# Revit family: Steel-HST Purlin-Steel & Tube-G450
name_source: partatom
category: Structural Framing
revit_build: Autodesk Revit 2018 (Build: 20170927_1515(x64)
units: mm (PartAtom-declared; Revit-internal decimal feet)

## family parameters
Always export as geometry = No
Always vertical = Yes
Cut with Voids When Loaded = No
Material for Model Behavior = Steel
OmniClass Number = 23.25.30.11.14.14
OmniClass Title = Beams
Section Shape = C Profile with Fold
Shared = No
Show family pre-cut in plan views = Yes
Structural Framing Length Roundoff = 0 mm

## types (13) — shared parameters
Assembly Code = B1020230
CBICode = 3411
CBIDescription = Structural steelwork
Coil Performance = Gauge 1.15-1.45mm; G500(MPa); 275g/m² (Zinc): Gauge 1.75-3.0mm; G450 (MPa); 275g/m²(Zinc)
Description = HST Steel Purlins and Girts are high strength lipped profile sections, providing an economic solution for your building project.
Design Instruction = All the design information should be cross referenced with the current Steel & Tube Purlins and Girts design guide, and AS/NZS 4600:2005
Design Standard = Steel & Tube’s HST purlins and Girts profiles are designed in accordance with AS/NZS 4600:2005.
Inner Fillet = 5.0 mm
Manufacturer = Steel & Tube
ManufacturerName = Steel & Tube
ManufacturerURL = http://www.steelandtube.co.nz
Material Standard = Steel & Tube’s HST purlins and Girts profiles are manufactured from materials conforming to AS1397:2011
ModifiedIssue_ANZRS = 20160330 $
Perimeter = 0.00 m²/m
Principal Axes Angle = 0.00°
Profile2 Height Validation = 152 mm  [stored 0.498688 ft]
SpecificationDescription = Steel & Tube Purlins & Girts
SpecificationReference = 3411ST
Torsional Modulus = 0.0 mm³
Type Comments = HST Steel Purlins and Girts
URL = http://www.steelandtube.co.nz
Uniclass2015Code = Pr_20_76_51_21
Uniclass2015Title = Cold-formed galvanized steel sections
Uniclass2015Version = 2015

## per-type parameters (varying)
- HST100/19: Centroid Horizontal=16.4 mm; Centroid Vertical=51.0 mm; Elastic Modulus strong axis=13140.0 mm³; Elastic Modulus weak axis=4290.0 mm³; Fold Length=10.0 mm; Height=102.0 mm; Lip Length=15.0 mm; MassPerUnitLength_ANZRS=3.23 kg/m; Moment of Inertia strong axis=658000.00 mm4; Moment of Inertia weak axis=141000.00 mm4; Nominal Weight=3.23 kgf/m; Plastic Modulus strong axis=13140.0 mm³; Plastic Modulus weak axis=4290.0 mm³; Profile1=Yes; Profile2=No; Profile23Medium=No; Profile3=No; Profile3 Height Validation=203 mm  [stored 0.66601 ft]; Section Area=400.0 mm²; SectionAreaGross_ANZRS=400.0 mm²; SectionAreaNet_ANZRS=400.0 mm²; Shear Area strong axis=400.0 mm²; Shear Area weak axis=400.0 mm²; Structural Material=Metal-Steel-450MPa; Torsional Moment of Inertia=456.00 mm4; Wall Design Thickness=1.9 mm; Wall Nominal Thickness=1.9 mm; Warping Constant=310000000.0 mm6; Width=51.0 mm; b1=8.0 mm; d1=59.0 mm; d2=10.0 mm; d3=25.0 mm; d4=48.0 mm
- HST150/18: Centroid Horizontal=23.0 mm; Centroid Vertical=76.0 mm; Elastic Modulus strong axis=27000.0 mm³; Elastic Modulus weak axis=9010.0 mm³; Fold Length=10.0 mm; Height=152.0 mm; Lip Length=24.0 mm; MassPerUnitLength_ANZRS=4.56 kg/m; Moment of Inertia strong axis=2050000.00 mm4; Moment of Inertia weak axis=364000.00 mm4; Nominal Weight=4.56 kgf/m; Plastic Modulus strong axis=27000.0 mm³; Plastic Modulus weak axis=9010.0 mm³; Profile1=No; Profile2=Yes; Profile23Medium=Yes; Profile3=No; Profile3 Height Validation=203 mm  [stored 0.66601 ft]; Section Area=578.0 mm²; SectionAreaGross_ANZRS=578.0 mm²; SectionAreaNet_ANZRS=578.0 mm²; Shear Area strong axis=578.0 mm²; Shear Area weak axis=578.0 mm²; Structural Material=Metal-Steel-450MPa; Torsional Moment of Inertia=590.00 mm4; Wall Design Thickness=1.8 mm; Wall Nominal Thickness=1.8 mm; Warping Constant=2190000000.0 mm6; Width=65.0 mm; b1=8.0 mm; d1=59.0 mm; d2=10.0 mm; d3=7.0 mm; d4=48.0 mm
- HST200/18: Centroid Horizontal=24.6 mm; Centroid Vertical=101.5 mm; Elastic Modulus strong axis=44200.0 mm³; Elastic Modulus weak axis=11900.0 mm³; Fold Length=12.0 mm; Height=203.0 mm; Lip Length=25.0 mm; MassPerUnitLength_ANZRS=5.72 kg/m; Moment of Inertia strong axis=4480000.00 mm4; Moment of Inertia weak axis=577000.00 mm4; Nominal Weight=5.72 kgf/m; Plastic Modulus strong axis=44200.0 mm³; Plastic Modulus weak axis=11900.0 mm³; Profile1=No; Profile2=No; Profile23Medium=Yes; Profile3=Yes; Profile3 Height Validation=203 mm  [stored 0.66601 ft]; Section Area=717.0 mm²; SectionAreaGross_ANZRS=717.0 mm²; SectionAreaNet_ANZRS=717.0 mm²; Shear Area strong axis=717.0 mm²; Shear Area weak axis=717.0 mm²; Structural Material=Metal-Steel-450MPa; Torsional Moment of Inertia=732.00 mm4; Wall Design Thickness=1.8 mm; Wall Nominal Thickness=1.8 mm; Warping Constant=5670000000.0 mm6; Width=75.0 mm; b1=8.0 mm; d1=59.0 mm; d2=10.0 mm; d3=10.0 mm; d4=48.0 mm
- HST250/18: Centroid Horizontal=28.3 mm; Centroid Vertical=125.0 mm; Elastic Modulus strong axis=64700.0 mm³; Elastic Modulus weak axis=16300.0 mm³; Fold Length=12.0 mm; Height=250.0 mm; Lip Length=33.0 mm; MassPerUnitLength_ANZRS=6.96 kg/m; Moment of Inertia strong axis=8090000.00 mm4; Moment of Inertia weak axis=897000.00 mm4; Nominal Weight=6.96 kgf/m; Plastic Modulus strong axis=64700.0 mm³; Plastic Modulus weak axis=16300.0 mm³; Profile1=No; Profile2=No; Profile23Medium=Yes; Profile3=Yes; Profile3 Height Validation=250 mm; Section Area=866.0 mm²; SectionAreaGross_ANZRS=866.0 mm²; SectionAreaNet_ANZRS=866.0 mm²; Shear Area strong axis=866.0 mm²; Shear Area weak axis=866.0 mm²; Structural Material=Metal-Steel-450MPa; Torsional Moment of Inertia=885.00 mm4; Wall Design Thickness=1.8 mm; Wall Nominal Thickness=1.8 mm; Warping Constant=14000000000.0 mm6; Width=85.0 mm; b1=10.0 mm; d1=59.0 mm; d2=14.0 mm; d3=25.0 mm; d4=73.0 mm
- HST300/18: Centroid Horizontal=31.9 mm; Centroid Vertical=150.0 mm; Elastic Modulus strong axis=91600.0 mm³; Elastic Modulus weak axis=22000.0 mm³; Fold Length=12.0 mm; Height=300.0 mm; Lip Length=38.0 mm; MassPerUnitLength_ANZRS=8.08 kg/m; Moment of Inertia strong axis=13700000.00 mm4; Moment of Inertia weak axis=1460000.00 mm4; Nominal Weight=8.08 kgf/m; Plastic Modulus strong axis=91600.0 mm³; Plastic Modulus weak axis=22000.0 mm³; Profile1=No; Profile2=No; Profile23Medium=Yes; Profile3=Yes; Profile3 Height Validation=300 mm; Section Area=1018.0 mm²; SectionAreaGross_ANZRS=1018.0 mm²; SectionAreaNet_ANZRS=1018.0 mm²; Shear Area strong axis=1018.0 mm²; Shear Area weak axis=1018.0 mm²; Structural Material=Metal-Steel-450MPa; Torsional Moment of Inertia=1039.00 mm4; Wall Design Thickness=1.8 mm; Wall Nominal Thickness=1.8 mm; Warping Constant=31200000000.0 mm6; Width=100.0 mm; b1=10.0 mm; d1=59.0 mm; d2=64.0 mm; d3=25.0 mm; d4=123.0 mm
- HST300/24: Centroid Horizontal=31.4 mm; Centroid Vertical=150.0 mm; Elastic Modulus strong axis=124000.0 mm³; Elastic Modulus weak axis=29500.0 mm³; Fold Length=12.0 mm; Height=300.0 mm; Lip Length=38.0 mm; MassPerUnitLength_ANZRS=11.01 kg/m; Moment of Inertia strong axis=18600000.00 mm4; Moment of Inertia weak axis=1950000.00 mm4; Nominal Weight=11.01 kgf/m; Plastic Modulus strong axis=124000.0 mm³; Plastic Modulus weak axis=29500.0 mm³; Profile1=No; Profile2=No; Profile23Medium=Yes; Profile3=Yes; Profile3 Height Validation=300 mm; Section Area=1382.0 mm²; SectionAreaGross_ANZRS=1382.0 mm²; SectionAreaNet_ANZRS=1382.0 mm²; Shear Area strong axis=1382.0 mm²; Shear Area weak axis=1382.0 mm²; Structural Material=Metal-Steel-450MPa; Torsional Moment of Inertia=2653.00 mm4; Wall Design Thickness=2.4 mm; Wall Nominal Thickness=2.4 mm; Warping Constant=41100000000.0 mm6; Width=100.0 mm; b1=10.0 mm; d1=59.0 mm; d2=64.0 mm; d3=25.0 mm; d4=123.0 mm
- HST300/30: Centroid Horizontal=30.9 mm; Centroid Vertical=150.0 mm; Elastic Modulus strong axis=153000.0 mm³; Elastic Modulus weak axis=36000.0 mm³; Fold Length=12.0 mm; Height=300.0 mm; Lip Length=38.0 mm; MassPerUnitLength_ANZRS=13.71 kg/m; Moment of Inertia strong axis=22900000.00 mm4; Moment of Inertia weak axis=2380000.00 mm4; Nominal Weight=13.71 kgf/m; Plastic Modulus strong axis=153000.0 mm³; Plastic Modulus weak axis=36000.0 mm³; Profile1=No; Profile2=No; Profile23Medium=Yes; Profile3=Yes; Profile3 Height Validation=300 mm; Section Area=1711.0 mm²; SectionAreaGross_ANZRS=1711.0 mm²; SectionAreaNet_ANZRS=1711.0 mm²; Shear Area strong axis=1711.0 mm²; Shear Area weak axis=1711.0 mm²; Structural Material=Metal-Steel-450MPa; Torsional Moment of Inertia=5134.00 mm4; Wall Design Thickness=3.0 mm; Wall Nominal Thickness=3.0 mm; Warping Constant=49400000000.0 mm6; Width=100.0 mm; b1=10.0 mm; d1=59.0 mm; d2=64.0 mm; d3=25.0 mm; d4=123.0 mm
- HST350/18: Centroid Horizontal=30.4 mm; Centroid Vertical=175.0 mm; Elastic Modulus strong axis=115000.0 mm³; Elastic Modulus weak axis=24000.0 mm³; Fold Length=12.0 mm; Height=350.0 mm; Lip Length=43.0 mm; MassPerUnitLength_ANZRS=8.96 kg/m; Moment of Inertia strong axis=20100000.00 mm4; Moment of Inertia weak axis=1630000.00 mm4; Nominal Weight=8.96 kgf/m; Plastic Modulus strong axis=115000.0 mm³; Plastic Modulus weak axis=24000.0 mm³; Profile1=No; Profile2=No; Profile23Medium=Yes; Profile3=Yes; Profile3 Height Validation=350 mm; Section Area=1123.0 mm²; SectionAreaGross_ANZRS=1123.0 mm²; SectionAreaNet_ANZRS=1123.0 mm²; Shear Area strong axis=1123.0 mm²; Shear Area weak axis=1123.0 mm²; Structural Material=Metal-Steel-450MPa; Torsional Moment of Inertia=1146.00 mm4; Wall Design Thickness=1.8 mm; Wall Nominal Thickness=1.8 mm; Warping Constant=46700000000.0 mm6; Width=100.0 mm; b1=10.0 mm; d1=70.0 mm; d2=92.0 mm; d3=25.0 mm; d4=151.0 mm
- HST350/24: Centroid Horizontal=29.9 mm; Centroid Vertical=175.0 mm; Elastic Modulus strong axis=155000.0 mm³; Elastic Modulus weak axis=32100.0 mm³; Fold Length=12.0 mm; Height=350.0 mm; Lip Length=43.0 mm; MassPerUnitLength_ANZRS=12.08 kg/m; Moment of Inertia strong axis=27200000.00 mm4; Moment of Inertia weak axis=2170000.00 mm4; Nominal Weight=12.08 kgf/m; Plastic Modulus strong axis=155000.0 mm³; Plastic Modulus weak axis=32100.0 mm³; Profile1=No; Profile2=No; Profile23Medium=Yes; Profile3=Yes; Profile3 Height Validation=350 mm; Section Area=1526.0 mm²; SectionAreaGross_ANZRS=1526.0 mm²; SectionAreaNet_ANZRS=1526.0 mm²; Shear Area strong axis=1526.0 mm²; Shear Area weak axis=1526.0 mm²; Structural Material=Metal-Steel-500MPa; Torsional Moment of Inertia=2930.00 mm4; Wall Design Thickness=2.4 mm; Wall Nominal Thickness=2.4 mm; Warping Constant=61600000000.0 mm6; Width=100.0 mm; b1=10.0 mm; d1=70.0 mm; d2=92.0 mm; d3=25.0 mm; d4=151.0 mm
- HST350/30: Centroid Horizontal=29.5 mm; Centroid Vertical=175.0 mm; Elastic Modulus strong axis=192000.0 mm³; Elastic Modulus weak axis=39300.0 mm³; Fold Length=12.0 mm; Height=350.0 mm; Lip Length=43.0 mm; MassPerUnitLength_ANZRS=15.05 kg/m; Moment of Inertia strong axis=33500000.00 mm4; Moment of Inertia weak axis=2650000.00 mm4; Nominal Weight=15.05 kgf/m; Plastic Modulus strong axis=192000.0 mm³; Plastic Modulus weak axis=39300.0 mm³; Profile1=No; Profile2=No; Profile23Medium=Yes; Profile3=Yes; Profile3 Height Validation=350 mm; Section Area=1891.0 mm²; SectionAreaGross_ANZRS=1891.0 mm²; SectionAreaNet_ANZRS=1891.0 mm²; Shear Area strong axis=1891.0 mm²; Shear Area weak axis=1891.0 mm²; Structural Material=Metal-Steel-500MPa; Torsional Moment of Inertia=5674.00 mm4; Wall Design Thickness=3.0 mm; Wall Nominal Thickness=3.0 mm; Warping Constant=74300000000.0 mm6; Width=100.0 mm; b1=10.0 mm; d1=70.0 mm; d2=92.0 mm; d3=25.0 mm; d4=151.0 mm
- HST400/20: Centroid Horizontal=29.1 mm; Centroid Vertical=200.0 mm; Elastic Modulus strong axis=155000.0 mm³; Elastic Modulus weak axis=28600.0 mm³; Fold Length=12.0 mm; Height=400.0 mm; Lip Length=48.0 mm; MassPerUnitLength_ANZRS=10.78 kg/m; Moment of Inertia strong axis=31100000.00 mm4; Moment of Inertia weak axis=1970000.00 mm4; Nominal Weight=10.78 kgf/m; Plastic Modulus strong axis=155000.0 mm³; Plastic Modulus weak axis=28600.0 mm³; Profile1=No; Profile2=No; Profile23Medium=Yes; Profile3=Yes; Profile3 Height Validation=400 mm  [stored 1.31234 ft]; Section Area=1365.0 mm²; SectionAreaGross_ANZRS=1365.0 mm²; SectionAreaNet_ANZRS=1365.0 mm²; Shear Area strong axis=1365.0 mm²; Shear Area weak axis=1365.0 mm²; Structural Material=Metal-Steel-450MPa; Torsional Moment of Inertia=1730.00 mm4; Wall Design Thickness=2.0 mm; Wall Nominal Thickness=2.0 mm; Warping Constant=73100000000.0 mm6; Width=100.0 mm; b1=10.0 mm; d1=75.0 mm; d2=132.0 mm; d3=25.0 mm; d4=191.0 mm
- HST400/24: Centroid Horizontal=28.8 mm; Centroid Vertical=200.0 mm; Elastic Modulus strong axis=190000.0 mm³; Elastic Modulus weak axis=34700.0 mm³; Fold Length=12.0 mm; Height=400.0 mm; Lip Length=48.0 mm; MassPerUnitLength_ANZRS=13.23 kg/m; Moment of Inertia strong axis=37900000.00 mm4; Moment of Inertia weak axis=2390000.00 mm4; Nominal Weight=13.23 kgf/m; Plastic Modulus strong axis=190000.0 mm³; Plastic Modulus weak axis=34700.0 mm³; Profile1=No; Profile2=No; Profile23Medium=Yes; Profile3=Yes; Profile3 Height Validation=400 mm  [stored 1.31234 ft]; Section Area=1670.0 mm²; SectionAreaGross_ANZRS=1670.0 mm²; SectionAreaNet_ANZRS=1670.0 mm²; Shear Area strong axis=1670.0 mm²; Shear Area weak axis=1670.0 mm²; Structural Material=Metal-Steel-450MPa; Torsional Moment of Inertia=3206.00 mm4; Wall Design Thickness=2.4 mm; Wall Nominal Thickness=2.4 mm; Warping Constant=87700000000.0 mm6; Width=100.0 mm; b1=10.0 mm; d1=75.0 mm; d2=132.0 mm; d3=25.0 mm; d4=191.0 mm
- HST400/30: Centroid Horizontal=28.3 mm; Centroid Vertical=200.0 mm; Elastic Modulus strong axis=234000.0 mm³; Elastic Modulus weak axis=42500.0 mm³; Fold Length=12.0 mm; Height=400.0 mm; Lip Length=48.0 mm; MassPerUnitLength_ANZRS=16.48 kg/m; Moment of Inertia strong axis=46900000.00 mm4; Moment of Inertia weak axis=2920000.00 mm4; Nominal Weight=16.48 kgf/m; Plastic Modulus strong axis=234000.0 mm³; Plastic Modulus weak axis=42500.0 mm³; Profile1=No; Profile2=No; Profile23Medium=Yes; Profile3=Yes; Profile3 Height Validation=400 mm  [stored 1.31234 ft]; Section Area=2071.0 mm²; SectionAreaGross_ANZRS=2071.0 mm²; SectionAreaNet_ANZRS=2071.0 mm²; Shear Area strong axis=2071.0 mm²; Shear Area weak axis=2071.0 mm²; Structural Material=Metal-Steel-450MPa; Torsional Moment of Inertia=6214.00 mm4; Wall Design Thickness=3.0 mm; Wall Nominal Thickness=3.0 mm; Warping Constant=106000000000.0 mm6; Width=100.0 mm; b1=10.0 mm; d1=75.0 mm; d2=132.0 mm; d3=25.0 mm; d4=191.0 mm

note: column(s) folded — value = type name in every type: Model

note: [stored X ft] marks values corroborated as IEEE doubles in the binary element streams (Revit-internal decimal feet)

## geometry (parser evidence)
native form markers: Sweep x6
no freeform markers — native parametric forms only
